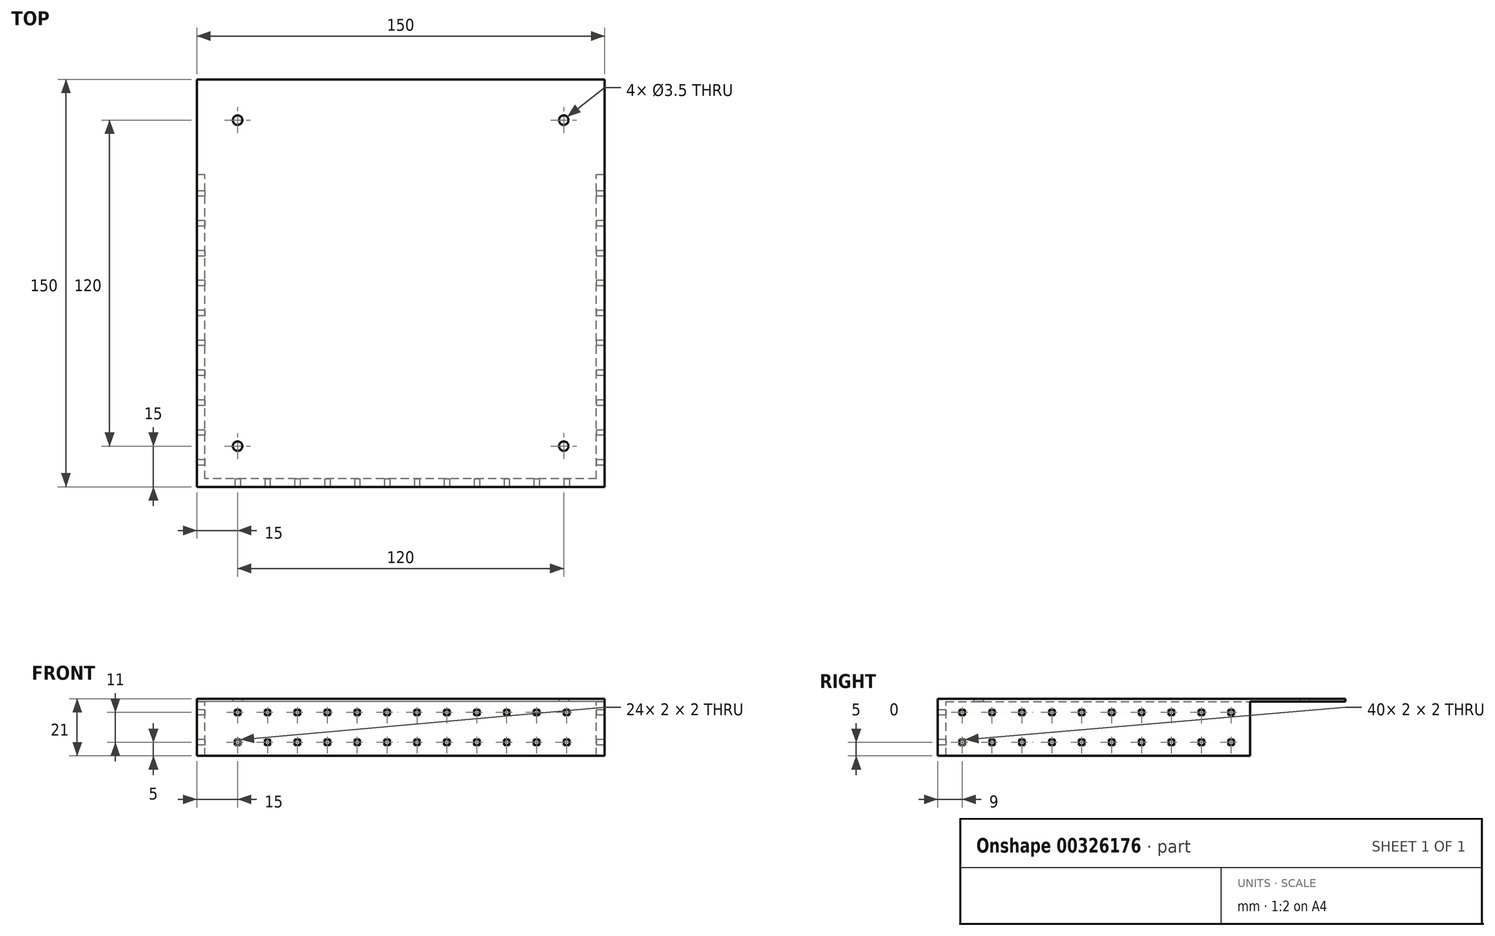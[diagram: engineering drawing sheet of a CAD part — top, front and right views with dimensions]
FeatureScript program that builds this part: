
annotation { "Feature Type Name" : "Feature", "Feature Type Description" : "" }
export const myFeature = defineFeature(function(context is Context, id is Id, definition is map)
    precondition{}
    {
        {
            var Q0;
            Q0=qCreatedBy(makeId("Top.planeOp"),FACE);
            var sketch = newSketch(context, id + "F0", { "sketchPlane" : qUnion([Q0]), "disableImprinting" : false});
            skLineSegment(sketch, "E0.bottom", {"start": v(60, -60) * mm, "end": v(-60, -60) * mm, "construction": true});
            skLineSegment(sketch, "E0.top", {"start": v(60, 60) * mm, "end": v(-60, 60) * mm, "construction": true});
            skLineSegment(sketch, "E0.left", {"start": v(60, -60) * mm, "end": v(60, 60) * mm, "construction": true});
            skLineSegment(sketch, "E0.right", {"start": v(-60, -60) * mm, "end": v(-60, 60) * mm, "construction": true});
            skCircle(sketch, "E1", {"center": v(60, -60) * mm, "radius": 1.75 * mm});
            skCircle(sketch, "E2.1.0", {"center": v(60, 60) * mm, "radius": 1.75 * mm});
            skCircle(sketch, "E2.2.0", {"center": v(-60, 60) * mm, "radius": 1.75 * mm});
            skCircle(sketch, "E2.3.0", {"center": v(-60, -60) * mm, "radius": 1.75 * mm});
            skLineSegment(sketch, "E3.bottom", {"start": v(75, -75) * mm, "end": v(-75, -75) * mm});
            skLineSegment(sketch, "E3.top", {"start": v(75, 75) * mm, "end": v(-75, 75) * mm});
            skLineSegment(sketch, "E3.left", {"start": v(75, -75) * mm, "end": v(75, 75) * mm});
            skLineSegment(sketch, "E3.right", {"start": v(-75, -75) * mm, "end": v(-75, 75) * mm});
            skLineSegment(sketch, "E4.bottom", {"start": v(72, -72) * mm, "end": v(-72, -72) * mm});
            skLineSegment(sketch, "E4.top", {"start": v(72, 72) * mm, "end": v(-72, 72) * mm});
            skLineSegment(sketch, "E4.left", {"start": v(72, -72) * mm, "end": v(72, 72) * mm});
            skLineSegment(sketch, "E4.right", {"start": v(-72, -72) * mm, "end": v(-72, 72) * mm});
            skLineSegment(sketch, "E5", {"start": v(-75, 0) * mm, "end": v(-72, 0) * mm});
            skLineSegment(sketch, "E6", {"start": v(72, 0) * mm, "end": v(75, 0) * mm});
            skLineSegment(sketch, "E7", {"start": v(-75, 40) * mm, "end": v(-72, 40) * mm});
            skLineSegment(sketch, "E8", {"start": v(72, 40) * mm, "end": v(75, 40) * mm});
            skSolve(sketch);
        }
        {
            var Q0;
            Q0=makeQuery(id+"F0.imprint","IMPRINT",FACE,{"disambiguationData":[TD([[makeQuery(id+"F0.imprint","IMPRINT",EDGE,{"derivedFrom":sQuery(id+"F0.wireOp",EDGE,"E1")}),-1.0]])]});
            var Q1;
            {var subQ2=sQuery(id+"F0.wireOp",EDGE,"E3.top");Q1=makeQuery(id+"F0.imprint","IMPRINT",FACE,{"disambiguationData":[TD([[makeQuery(id+"F0.imprint","IMPRINT",EDGE,{"derivedFrom":subQ2}),1.0]])]});}
            var Q2;
            {var subQ2=sQuery(id+"F0.wireOp",EDGE,"E3.bottom");Q2=makeQuery(id+"F0.imprint","IMPRINT",FACE,{"disambiguationData":[TD([[makeQuery(id+"F0.imprint","IMPRINT",EDGE,{"derivedFrom":subQ2}),-1.0]])]});}
            var Q3;
            {var subQ0=sQuery(id+"F0.wireOp",EDGE,"E5");Q3=makeQuery(id+"F0.imprint","IMPRINT",FACE,{"disambiguationData":[TD([[makeQuery(id+"F0.imprint","IMPRINT",EDGE,{"derivedFrom":subQ0}),1.0]])]});}
            var Q4;
            {var subQ0=sQuery(id+"F0.wireOp",EDGE,"E6");Q4=makeQuery(id+"F0.imprint","IMPRINT",FACE,{"disambiguationData":[TD([[makeQuery(id+"F0.imprint","IMPRINT",EDGE,{"derivedFrom":subQ0}),1.0]])]});}
            extrude(context, id + "F1", {"entities" : qUnion([Q0, Q1, Q2, Q3, Q4]), "depth" : 1 * mm});
        }
        {
            var Q0;
            {var subQ2=sQuery(id+"F0.wireOp",EDGE,"E3.bottom");Q0=makeQuery(id+"F0.imprint","IMPRINT",FACE,{"disambiguationData":[TD([[makeQuery(id+"F0.imprint","IMPRINT",EDGE,{"derivedFrom":subQ2}),-1.0]])]});}
            var Q1;
            {var subQ0=sQuery(id+"F0.wireOp",EDGE,"E6");Q1=makeQuery(id+"F0.imprint","IMPRINT",FACE,{"disambiguationData":[TD([[makeQuery(id+"F0.imprint","IMPRINT",EDGE,{"derivedFrom":subQ0}),1.0]])]});}
            var Q2;
            {var subQ0=sQuery(id+"F0.wireOp",EDGE,"E5");Q2=makeQuery(id+"F0.imprint","IMPRINT",FACE,{"disambiguationData":[TD([[makeQuery(id+"F0.imprint","IMPRINT",EDGE,{"derivedFrom":subQ0}),1.0]])]});}
            extrude(context, id + "F2", {"entities" : qUnion([Q0, Q1, Q2]), "operationType" : NewBodyOperationType.ADD, "oppositeDirection" : true, "depth" : 20 * mm});
        }
        {
            var Q0;
            {var subQ0=sQuery(id+"F0.wireOp",EDGE,"E3.right");Q0=makeQuery(id+"F2.boolean.opBoolean","MERGE",FACE,{"derivedFrom":[makeQuery(id+"F1.opExtrude","SWEPT_FACE",FACE,{"disambiguationData":[OSD([subQ0])]}),makeQuery(id+"F2.opExtrude","SWEPT_FACE",FACE,{"disambiguationData":[OSD([subQ0])]})]});}
            var sketch = newSketch(context, id + "F3", { "sketchPlane" : qUnion([Q0])});
            skLineSegment(sketch, "E9.bottom", {"start": v(-32, -5) * mm, "end": v(-34, -5) * mm});
            skLineSegment(sketch, "E9.top", {"start": v(-32, -3) * mm, "end": v(-34, -3) * mm});
            skLineSegment(sketch, "E9.left", {"start": v(-32, -5) * mm, "end": v(-32, -3) * mm});
            skLineSegment(sketch, "E9.right", {"start": v(-34, -5) * mm, "end": v(-34, -3) * mm});
            skPoint(sketch, "E9.middle", {"position": v(-33, -4) * mm});
            skLineSegment(sketch, "E10.0.1.0", {"start": v(-32, -16) * mm, "end": v(-32, -14) * mm});
            skLineSegment(sketch, "E10.0.1.1", {"start": v(-32, -14) * mm, "end": v(-34, -14) * mm});
            skLineSegment(sketch, "E10.0.1.2", {"start": v(-34, -16) * mm, "end": v(-34, -14) * mm});
            skLineSegment(sketch, "E10.0.1.3", {"start": v(-32, -16) * mm, "end": v(-34, -16) * mm});
            skLineSegment(sketch, "E10.1.0.0", {"start": v(-21, -5) * mm, "end": v(-21, -3) * mm});
            skLineSegment(sketch, "E10.1.0.1", {"start": v(-21, -3) * mm, "end": v(-23, -3) * mm});
            skLineSegment(sketch, "E10.1.0.2", {"start": v(-23, -5) * mm, "end": v(-23, -3) * mm});
            skLineSegment(sketch, "E10.1.0.3", {"start": v(-21, -5) * mm, "end": v(-23, -5) * mm});
            skLineSegment(sketch, "E10.1.1.0", {"start": v(-21, -16) * mm, "end": v(-21, -14) * mm});
            skLineSegment(sketch, "E10.1.1.1", {"start": v(-21, -14) * mm, "end": v(-23, -14) * mm});
            skLineSegment(sketch, "E10.1.1.2", {"start": v(-23, -16) * mm, "end": v(-23, -14) * mm});
            skLineSegment(sketch, "E10.1.1.3", {"start": v(-21, -16) * mm, "end": v(-23, -16) * mm});
            skLineSegment(sketch, "E10.2.0.0", {"start": v(-10, -5) * mm, "end": v(-10, -3) * mm});
            skLineSegment(sketch, "E10.2.0.1", {"start": v(-10, -3) * mm, "end": v(-12, -3) * mm});
            skLineSegment(sketch, "E10.2.0.2", {"start": v(-12, -5) * mm, "end": v(-12, -3) * mm});
            skLineSegment(sketch, "E10.2.0.3", {"start": v(-10, -5) * mm, "end": v(-12, -5) * mm});
            skLineSegment(sketch, "E10.2.1.0", {"start": v(-10, -16) * mm, "end": v(-10, -14) * mm});
            skLineSegment(sketch, "E10.2.1.1", {"start": v(-10, -14) * mm, "end": v(-12, -14) * mm});
            skLineSegment(sketch, "E10.2.1.2", {"start": v(-12, -16) * mm, "end": v(-12, -14) * mm});
            skLineSegment(sketch, "E10.2.1.3", {"start": v(-10, -16) * mm, "end": v(-12, -16) * mm});
            skLineSegment(sketch, "E10.3.0.0", {"start": v(1, -5) * mm, "end": v(1, -3) * mm});
            skLineSegment(sketch, "E10.3.0.1", {"start": v(1, -3) * mm, "end": v(-1, -3) * mm});
            skLineSegment(sketch, "E10.3.0.2", {"start": v(-1, -5) * mm, "end": v(-1, -3) * mm});
            skLineSegment(sketch, "E10.3.0.3", {"start": v(1, -5) * mm, "end": v(-1, -5) * mm});
            skLineSegment(sketch, "E10.3.1.0", {"start": v(1, -16) * mm, "end": v(1, -14) * mm});
            skLineSegment(sketch, "E10.3.1.1", {"start": v(1, -14) * mm, "end": v(-1, -14) * mm});
            skLineSegment(sketch, "E10.3.1.2", {"start": v(-1, -16) * mm, "end": v(-1, -14) * mm});
            skLineSegment(sketch, "E10.3.1.3", {"start": v(1, -16) * mm, "end": v(-1, -16) * mm});
            skLineSegment(sketch, "E10.4.0.0", {"start": v(12, -5) * mm, "end": v(12, -3) * mm});
            skLineSegment(sketch, "E10.4.0.1", {"start": v(12, -3) * mm, "end": v(10, -3) * mm});
            skLineSegment(sketch, "E10.4.0.2", {"start": v(10, -5) * mm, "end": v(10, -3) * mm});
            skLineSegment(sketch, "E10.4.0.3", {"start": v(12, -5) * mm, "end": v(10, -5) * mm});
            skLineSegment(sketch, "E10.4.1.0", {"start": v(12, -16) * mm, "end": v(12, -14) * mm});
            skLineSegment(sketch, "E10.4.1.1", {"start": v(12, -14) * mm, "end": v(10, -14) * mm});
            skLineSegment(sketch, "E10.4.1.2", {"start": v(10, -16) * mm, "end": v(10, -14) * mm});
            skLineSegment(sketch, "E10.4.1.3", {"start": v(12, -16) * mm, "end": v(10, -16) * mm});
            skLineSegment(sketch, "E10.5.0.0", {"start": v(23, -5) * mm, "end": v(23, -3) * mm});
            skLineSegment(sketch, "E10.5.0.1", {"start": v(23, -3) * mm, "end": v(21, -3) * mm});
            skLineSegment(sketch, "E10.5.0.2", {"start": v(21, -5) * mm, "end": v(21, -3) * mm});
            skLineSegment(sketch, "E10.5.0.3", {"start": v(23, -5) * mm, "end": v(21, -5) * mm});
            skLineSegment(sketch, "E10.5.1.0", {"start": v(23, -16) * mm, "end": v(23, -14) * mm});
            skLineSegment(sketch, "E10.5.1.1", {"start": v(23, -14) * mm, "end": v(21, -14) * mm});
            skLineSegment(sketch, "E10.5.1.2", {"start": v(21, -16) * mm, "end": v(21, -14) * mm});
            skLineSegment(sketch, "E10.5.1.3", {"start": v(23, -16) * mm, "end": v(21, -16) * mm});
            skLineSegment(sketch, "E10.6.0.0", {"start": v(34, -5) * mm, "end": v(34, -3) * mm});
            skLineSegment(sketch, "E10.6.0.1", {"start": v(34, -3) * mm, "end": v(32, -3) * mm});
            skLineSegment(sketch, "E10.6.0.2", {"start": v(32, -5) * mm, "end": v(32, -3) * mm});
            skLineSegment(sketch, "E10.6.0.3", {"start": v(34, -5) * mm, "end": v(32, -5) * mm});
            skLineSegment(sketch, "E10.6.1.0", {"start": v(34, -16) * mm, "end": v(34, -14) * mm});
            skLineSegment(sketch, "E10.6.1.1", {"start": v(34, -14) * mm, "end": v(32, -14) * mm});
            skLineSegment(sketch, "E10.6.1.2", {"start": v(32, -16) * mm, "end": v(32, -14) * mm});
            skLineSegment(sketch, "E10.6.1.3", {"start": v(34, -16) * mm, "end": v(32, -16) * mm});
            skLineSegment(sketch, "E10.7.0.0", {"start": v(45, -5) * mm, "end": v(45, -3) * mm});
            skLineSegment(sketch, "E10.7.0.1", {"start": v(45, -3) * mm, "end": v(43, -3) * mm});
            skLineSegment(sketch, "E10.7.0.2", {"start": v(43, -5) * mm, "end": v(43, -3) * mm});
            skLineSegment(sketch, "E10.7.0.3", {"start": v(45, -5) * mm, "end": v(43, -5) * mm});
            skLineSegment(sketch, "E10.7.1.0", {"start": v(45, -16) * mm, "end": v(45, -14) * mm});
            skLineSegment(sketch, "E10.7.1.1", {"start": v(45, -14) * mm, "end": v(43, -14) * mm});
            skLineSegment(sketch, "E10.7.1.2", {"start": v(43, -16) * mm, "end": v(43, -14) * mm});
            skLineSegment(sketch, "E10.7.1.3", {"start": v(45, -16) * mm, "end": v(43, -16) * mm});
            skLineSegment(sketch, "E10.8.0.0", {"start": v(56, -5) * mm, "end": v(56, -3) * mm});
            skLineSegment(sketch, "E10.8.0.1", {"start": v(56, -3) * mm, "end": v(54, -3) * mm});
            skLineSegment(sketch, "E10.8.0.2", {"start": v(54, -5) * mm, "end": v(54, -3) * mm});
            skLineSegment(sketch, "E10.8.0.3", {"start": v(56, -5) * mm, "end": v(54, -5) * mm});
            skLineSegment(sketch, "E10.8.1.0", {"start": v(56, -16) * mm, "end": v(56, -14) * mm});
            skLineSegment(sketch, "E10.8.1.1", {"start": v(56, -14) * mm, "end": v(54, -14) * mm});
            skLineSegment(sketch, "E10.8.1.2", {"start": v(54, -16) * mm, "end": v(54, -14) * mm});
            skLineSegment(sketch, "E10.8.1.3", {"start": v(56, -16) * mm, "end": v(54, -16) * mm});
            skLineSegment(sketch, "E10.9.0.0", {"start": v(67, -5) * mm, "end": v(67, -3) * mm});
            skLineSegment(sketch, "E10.9.0.1", {"start": v(67, -3) * mm, "end": v(65, -3) * mm});
            skLineSegment(sketch, "E10.9.0.2", {"start": v(65, -5) * mm, "end": v(65, -3) * mm});
            skLineSegment(sketch, "E10.9.0.3", {"start": v(67, -5) * mm, "end": v(65, -5) * mm});
            skLineSegment(sketch, "E10.9.1.0", {"start": v(67, -16) * mm, "end": v(67, -14) * mm});
            skLineSegment(sketch, "E10.9.1.1", {"start": v(67, -14) * mm, "end": v(65, -14) * mm});
            skLineSegment(sketch, "E10.9.1.2", {"start": v(65, -16) * mm, "end": v(65, -14) * mm});
            skLineSegment(sketch, "E10.9.1.3", {"start": v(67, -16) * mm, "end": v(65, -16) * mm});
            skLineSegment(sketch, "E10.direction1", {"start": v(-32, -5) * mm, "end": v(-21, -5) * mm, "construction": true});
            skLineSegment(sketch, "E10.direction2", {"start": v(-32, -5) * mm, "end": v(-32, -16) * mm, "construction": true});
            skSolve(sketch);
        }
        {
            var Q0;
            Q0=makeQuery(id+"F3.imprint","IMPRINT",FACE,{"disambiguationData":[TD([[makeQuery(id+"F3.imprint","IMPRINT",EDGE,{"derivedFrom":sQuery(id+"F3.wireOp",EDGE,"E9.bottom")}),-1.0]])]});
            var Q1;
            Q1=makeQuery(id+"F3.imprint","IMPRINT",FACE,{"disambiguationData":[TD([[makeQuery(id+"F3.imprint","IMPRINT",EDGE,{"derivedFrom":sQuery(id+"F3.wireOp",EDGE,"E10.0.1.0")}),1.0]])]});
            var Q2;
            Q2=makeQuery(id+"F3.imprint","IMPRINT",FACE,{"disambiguationData":[TD([[makeQuery(id+"F3.imprint","IMPRINT",EDGE,{"derivedFrom":sQuery(id+"F3.wireOp",EDGE,"E10.1.0.0")}),1.0]])]});
            var Q3;
            Q3=makeQuery(id+"F3.imprint","IMPRINT",FACE,{"disambiguationData":[TD([[makeQuery(id+"F3.imprint","IMPRINT",EDGE,{"derivedFrom":sQuery(id+"F3.wireOp",EDGE,"E10.2.0.0")}),1.0]])]});
            var Q4;
            Q4=makeQuery(id+"F3.imprint","IMPRINT",FACE,{"disambiguationData":[TD([[makeQuery(id+"F3.imprint","IMPRINT",EDGE,{"derivedFrom":sQuery(id+"F3.wireOp",EDGE,"E10.2.1.0")}),1.0]])]});
            var Q5;
            Q5=makeQuery(id+"F3.imprint","IMPRINT",FACE,{"disambiguationData":[TD([[makeQuery(id+"F3.imprint","IMPRINT",EDGE,{"derivedFrom":sQuery(id+"F3.wireOp",EDGE,"E10.1.1.0")}),1.0]])]});
            var Q6;
            Q6=makeQuery(id+"F3.imprint","IMPRINT",FACE,{"disambiguationData":[TD([[makeQuery(id+"F3.imprint","IMPRINT",EDGE,{"derivedFrom":sQuery(id+"F3.wireOp",EDGE,"E10.3.1.0")}),1.0]])]});
            var Q7;
            Q7=makeQuery(id+"F3.imprint","IMPRINT",FACE,{"disambiguationData":[TD([[makeQuery(id+"F3.imprint","IMPRINT",EDGE,{"derivedFrom":sQuery(id+"F3.wireOp",EDGE,"E10.4.1.0")}),1.0]])]});
            var Q8;
            Q8=makeQuery(id+"F3.imprint","IMPRINT",FACE,{"disambiguationData":[TD([[makeQuery(id+"F3.imprint","IMPRINT",EDGE,{"derivedFrom":sQuery(id+"F3.wireOp",EDGE,"E10.5.1.0")}),1.0]])]});
            var Q9;
            Q9=makeQuery(id+"F3.imprint","IMPRINT",FACE,{"disambiguationData":[TD([[makeQuery(id+"F3.imprint","IMPRINT",EDGE,{"derivedFrom":sQuery(id+"F3.wireOp",EDGE,"E10.6.1.0")}),1.0]])]});
            var Q10;
            Q10=makeQuery(id+"F3.imprint","IMPRINT",FACE,{"disambiguationData":[TD([[makeQuery(id+"F3.imprint","IMPRINT",EDGE,{"derivedFrom":sQuery(id+"F3.wireOp",EDGE,"E10.7.1.0")}),1.0]])]});
            var Q11;
            Q11=makeQuery(id+"F3.imprint","IMPRINT",FACE,{"disambiguationData":[TD([[makeQuery(id+"F3.imprint","IMPRINT",EDGE,{"derivedFrom":sQuery(id+"F3.wireOp",EDGE,"E10.8.1.0")}),1.0]])]});
            var Q12;
            Q12=makeQuery(id+"F3.imprint","IMPRINT",FACE,{"disambiguationData":[TD([[makeQuery(id+"F3.imprint","IMPRINT",EDGE,{"derivedFrom":sQuery(id+"F3.wireOp",EDGE,"E10.9.1.0")}),1.0]])]});
            var Q13;
            Q13=makeQuery(id+"F3.imprint","IMPRINT",FACE,{"disambiguationData":[TD([[makeQuery(id+"F3.imprint","IMPRINT",EDGE,{"derivedFrom":sQuery(id+"F3.wireOp",EDGE,"E10.9.0.0")}),1.0]])]});
            var Q14;
            Q14=makeQuery(id+"F3.imprint","IMPRINT",FACE,{"disambiguationData":[TD([[makeQuery(id+"F3.imprint","IMPRINT",EDGE,{"derivedFrom":sQuery(id+"F3.wireOp",EDGE,"E10.8.0.0")}),1.0]])]});
            var Q15;
            Q15=makeQuery(id+"F3.imprint","IMPRINT",FACE,{"disambiguationData":[TD([[makeQuery(id+"F3.imprint","IMPRINT",EDGE,{"derivedFrom":sQuery(id+"F3.wireOp",EDGE,"E10.7.0.0")}),1.0]])]});
            var Q16;
            Q16=makeQuery(id+"F3.imprint","IMPRINT",FACE,{"disambiguationData":[TD([[makeQuery(id+"F3.imprint","IMPRINT",EDGE,{"derivedFrom":sQuery(id+"F3.wireOp",EDGE,"E10.6.0.0")}),1.0]])]});
            var Q17;
            Q17=makeQuery(id+"F3.imprint","IMPRINT",FACE,{"disambiguationData":[TD([[makeQuery(id+"F3.imprint","IMPRINT",EDGE,{"derivedFrom":sQuery(id+"F3.wireOp",EDGE,"E10.5.0.0")}),1.0]])]});
            var Q18;
            Q18=makeQuery(id+"F3.imprint","IMPRINT",FACE,{"disambiguationData":[TD([[makeQuery(id+"F3.imprint","IMPRINT",EDGE,{"derivedFrom":sQuery(id+"F3.wireOp",EDGE,"E10.4.0.0")}),1.0]])]});
            var Q19;
            Q19=makeQuery(id+"F3.imprint","IMPRINT",FACE,{"disambiguationData":[TD([[makeQuery(id+"F3.imprint","IMPRINT",EDGE,{"derivedFrom":sQuery(id+"F3.wireOp",EDGE,"E10.3.0.0")}),1.0]])]});
            extrude(context, id + "F4", {"entities" : qUnion([Q0, Q1, Q2, Q3, Q4, Q5, Q6, Q7, Q8, Q9, Q10, Q11, Q12, Q13, Q14, Q15, Q16, Q17, Q18, Q19]), "operationType" : NewBodyOperationType.REMOVE, "oppositeDirection" : true, "depth" : 200 * mm});
        }
        {
            var Q0;
            {var subQ0=sQuery(id+"F0.wireOp",EDGE,"E3.bottom");Q0=makeQuery(id+"F2.boolean.opBoolean","MERGE",FACE,{"derivedFrom":[makeQuery(id+"F1.opExtrude","SWEPT_FACE",FACE,{"disambiguationData":[OSD([subQ0])]}),makeQuery(id+"F2.opExtrude","SWEPT_FACE",FACE,{"disambiguationData":[OSD([subQ0])]})]});}
            var sketch = newSketch(context, id + "F5", { "sketchPlane" : qUnion([Q0])});
            skLineSegment(sketch, "E11.bottom", {"start": v(-59, -5) * mm, "end": v(-61, -5) * mm});
            skLineSegment(sketch, "E11.top", {"start": v(-59, -3) * mm, "end": v(-61, -3) * mm});
            skLineSegment(sketch, "E11.left", {"start": v(-59, -5) * mm, "end": v(-59, -3) * mm});
            skLineSegment(sketch, "E11.right", {"start": v(-61, -5) * mm, "end": v(-61, -3) * mm});
            skPoint(sketch, "E11.middle", {"position": v(-60, -4) * mm});
            skLineSegment(sketch, "E12.0.1.0", {"start": v(-59, -16) * mm, "end": v(-59, -14) * mm});
            skLineSegment(sketch, "E12.0.1.1", {"start": v(-59, -14) * mm, "end": v(-61, -14) * mm});
            skLineSegment(sketch, "E12.0.1.2", {"start": v(-61, -16) * mm, "end": v(-61, -14) * mm});
            skLineSegment(sketch, "E12.0.1.3", {"start": v(-59, -16) * mm, "end": v(-61, -16) * mm});
            skLineSegment(sketch, "E12.1.0.0", {"start": v(-48, -5) * mm, "end": v(-48, -3) * mm});
            skLineSegment(sketch, "E12.1.0.1", {"start": v(-48, -3) * mm, "end": v(-50, -3) * mm});
            skLineSegment(sketch, "E12.1.0.2", {"start": v(-50, -5) * mm, "end": v(-50, -3) * mm});
            skLineSegment(sketch, "E12.1.0.3", {"start": v(-48, -5) * mm, "end": v(-50, -5) * mm});
            skLineSegment(sketch, "E12.1.1.0", {"start": v(-48, -16) * mm, "end": v(-48, -14) * mm});
            skLineSegment(sketch, "E12.1.1.1", {"start": v(-48, -14) * mm, "end": v(-50, -14) * mm});
            skLineSegment(sketch, "E12.1.1.2", {"start": v(-50, -16) * mm, "end": v(-50, -14) * mm});
            skLineSegment(sketch, "E12.1.1.3", {"start": v(-48, -16) * mm, "end": v(-50, -16) * mm});
            skLineSegment(sketch, "E12.2.0.0", {"start": v(-37, -5) * mm, "end": v(-37, -3) * mm});
            skLineSegment(sketch, "E12.2.0.1", {"start": v(-37, -3) * mm, "end": v(-39, -3) * mm});
            skLineSegment(sketch, "E12.2.0.2", {"start": v(-39, -5) * mm, "end": v(-39, -3) * mm});
            skLineSegment(sketch, "E12.2.0.3", {"start": v(-37, -5) * mm, "end": v(-39, -5) * mm});
            skLineSegment(sketch, "E12.2.1.0", {"start": v(-37, -16) * mm, "end": v(-37, -14) * mm});
            skLineSegment(sketch, "E12.2.1.1", {"start": v(-37, -14) * mm, "end": v(-39, -14) * mm});
            skLineSegment(sketch, "E12.2.1.2", {"start": v(-39, -16) * mm, "end": v(-39, -14) * mm});
            skLineSegment(sketch, "E12.2.1.3", {"start": v(-37, -16) * mm, "end": v(-39, -16) * mm});
            skLineSegment(sketch, "E12.3.0.0", {"start": v(-26, -5) * mm, "end": v(-26, -3) * mm});
            skLineSegment(sketch, "E12.3.0.1", {"start": v(-26, -3) * mm, "end": v(-28, -3) * mm});
            skLineSegment(sketch, "E12.3.0.2", {"start": v(-28, -5) * mm, "end": v(-28, -3) * mm});
            skLineSegment(sketch, "E12.3.0.3", {"start": v(-26, -5) * mm, "end": v(-28, -5) * mm});
            skLineSegment(sketch, "E12.3.1.0", {"start": v(-26, -16) * mm, "end": v(-26, -14) * mm});
            skLineSegment(sketch, "E12.3.1.1", {"start": v(-26, -14) * mm, "end": v(-28, -14) * mm});
            skLineSegment(sketch, "E12.3.1.2", {"start": v(-28, -16) * mm, "end": v(-28, -14) * mm});
            skLineSegment(sketch, "E12.3.1.3", {"start": v(-26, -16) * mm, "end": v(-28, -16) * mm});
            skLineSegment(sketch, "E12.4.0.0", {"start": v(-15, -5) * mm, "end": v(-15, -3) * mm});
            skLineSegment(sketch, "E12.4.0.1", {"start": v(-15, -3) * mm, "end": v(-17, -3) * mm});
            skLineSegment(sketch, "E12.4.0.2", {"start": v(-17, -5) * mm, "end": v(-17, -3) * mm});
            skLineSegment(sketch, "E12.4.0.3", {"start": v(-15, -5) * mm, "end": v(-17, -5) * mm});
            skLineSegment(sketch, "E12.4.1.0", {"start": v(-15, -16) * mm, "end": v(-15, -14) * mm});
            skLineSegment(sketch, "E12.4.1.1", {"start": v(-15, -14) * mm, "end": v(-17, -14) * mm});
            skLineSegment(sketch, "E12.4.1.2", {"start": v(-17, -16) * mm, "end": v(-17, -14) * mm});
            skLineSegment(sketch, "E12.4.1.3", {"start": v(-15, -16) * mm, "end": v(-17, -16) * mm});
            skLineSegment(sketch, "E12.5.0.0", {"start": v(-4, -5) * mm, "end": v(-4, -3) * mm});
            skLineSegment(sketch, "E12.5.0.1", {"start": v(-4, -3) * mm, "end": v(-6, -3) * mm});
            skLineSegment(sketch, "E12.5.0.2", {"start": v(-6, -5) * mm, "end": v(-6, -3) * mm});
            skLineSegment(sketch, "E12.5.0.3", {"start": v(-4, -5) * mm, "end": v(-6, -5) * mm});
            skLineSegment(sketch, "E12.5.1.0", {"start": v(-4, -16) * mm, "end": v(-4, -14) * mm});
            skLineSegment(sketch, "E12.5.1.1", {"start": v(-4, -14) * mm, "end": v(-6, -14) * mm});
            skLineSegment(sketch, "E12.5.1.2", {"start": v(-6, -16) * mm, "end": v(-6, -14) * mm});
            skLineSegment(sketch, "E12.5.1.3", {"start": v(-4, -16) * mm, "end": v(-6, -16) * mm});
            skLineSegment(sketch, "E12.6.0.0", {"start": v(7, -5) * mm, "end": v(7, -3) * mm});
            skLineSegment(sketch, "E12.6.0.1", {"start": v(7, -3) * mm, "end": v(5, -3) * mm});
            skLineSegment(sketch, "E12.6.0.2", {"start": v(5, -5) * mm, "end": v(5, -3) * mm});
            skLineSegment(sketch, "E12.6.0.3", {"start": v(7, -5) * mm, "end": v(5, -5) * mm});
            skLineSegment(sketch, "E12.6.1.0", {"start": v(7, -16) * mm, "end": v(7, -14) * mm});
            skLineSegment(sketch, "E12.6.1.1", {"start": v(7, -14) * mm, "end": v(5, -14) * mm});
            skLineSegment(sketch, "E12.6.1.2", {"start": v(5, -16) * mm, "end": v(5, -14) * mm});
            skLineSegment(sketch, "E12.6.1.3", {"start": v(7, -16) * mm, "end": v(5, -16) * mm});
            skLineSegment(sketch, "E12.7.0.0", {"start": v(18, -5) * mm, "end": v(18, -3) * mm});
            skLineSegment(sketch, "E12.7.0.1", {"start": v(18, -3) * mm, "end": v(16, -3) * mm});
            skLineSegment(sketch, "E12.7.0.2", {"start": v(16, -5) * mm, "end": v(16, -3) * mm});
            skLineSegment(sketch, "E12.7.0.3", {"start": v(18, -5) * mm, "end": v(16, -5) * mm});
            skLineSegment(sketch, "E12.7.1.0", {"start": v(18, -16) * mm, "end": v(18, -14) * mm});
            skLineSegment(sketch, "E12.7.1.1", {"start": v(18, -14) * mm, "end": v(16, -14) * mm});
            skLineSegment(sketch, "E12.7.1.2", {"start": v(16, -16) * mm, "end": v(16, -14) * mm});
            skLineSegment(sketch, "E12.7.1.3", {"start": v(18, -16) * mm, "end": v(16, -16) * mm});
            skLineSegment(sketch, "E12.8.0.0", {"start": v(29, -5) * mm, "end": v(29, -3) * mm});
            skLineSegment(sketch, "E12.8.0.1", {"start": v(29, -3) * mm, "end": v(27, -3) * mm});
            skLineSegment(sketch, "E12.8.0.2", {"start": v(27, -5) * mm, "end": v(27, -3) * mm});
            skLineSegment(sketch, "E12.8.0.3", {"start": v(29, -5) * mm, "end": v(27, -5) * mm});
            skLineSegment(sketch, "E12.8.1.0", {"start": v(29, -16) * mm, "end": v(29, -14) * mm});
            skLineSegment(sketch, "E12.8.1.1", {"start": v(29, -14) * mm, "end": v(27, -14) * mm});
            skLineSegment(sketch, "E12.8.1.2", {"start": v(27, -16) * mm, "end": v(27, -14) * mm});
            skLineSegment(sketch, "E12.8.1.3", {"start": v(29, -16) * mm, "end": v(27, -16) * mm});
            skLineSegment(sketch, "E12.9.0.0", {"start": v(40, -5) * mm, "end": v(40, -3) * mm});
            skLineSegment(sketch, "E12.9.0.1", {"start": v(40, -3) * mm, "end": v(38, -3) * mm});
            skLineSegment(sketch, "E12.9.0.2", {"start": v(38, -5) * mm, "end": v(38, -3) * mm});
            skLineSegment(sketch, "E12.9.0.3", {"start": v(40, -5) * mm, "end": v(38, -5) * mm});
            skLineSegment(sketch, "E12.9.1.0", {"start": v(40, -16) * mm, "end": v(40, -14) * mm});
            skLineSegment(sketch, "E12.9.1.1", {"start": v(40, -14) * mm, "end": v(38, -14) * mm});
            skLineSegment(sketch, "E12.9.1.2", {"start": v(38, -16) * mm, "end": v(38, -14) * mm});
            skLineSegment(sketch, "E12.9.1.3", {"start": v(40, -16) * mm, "end": v(38, -16) * mm});
            skLineSegment(sketch, "E12.direction1", {"start": v(-59, -5) * mm, "end": v(-48, -5) * mm, "construction": true});
            skLineSegment(sketch, "E12.direction2", {"start": v(-59, -5) * mm, "end": v(-59, -16) * mm, "construction": true});
            skLineSegment(sketch, "E13.0.10.0", {"start": v(51, -5) * mm, "end": v(51, -3) * mm});
            skLineSegment(sketch, "E13.3.10.0", {"start": v(51, -3) * mm, "end": v(49, -3) * mm});
            skLineSegment(sketch, "E13.6.10.0", {"start": v(49, -5) * mm, "end": v(49, -3) * mm});
            skLineSegment(sketch, "E13.9.10.0", {"start": v(51, -5) * mm, "end": v(49, -5) * mm});
            skLineSegment(sketch, "E13.0.10.1", {"start": v(51, -16) * mm, "end": v(51, -14) * mm});
            skLineSegment(sketch, "E13.3.10.1", {"start": v(51, -14) * mm, "end": v(49, -14) * mm});
            skLineSegment(sketch, "E13.6.10.1", {"start": v(49, -16) * mm, "end": v(49, -14) * mm});
            skLineSegment(sketch, "E13.9.10.1", {"start": v(51, -16) * mm, "end": v(49, -16) * mm});
            skLineSegment(sketch, "E14.0.11.0", {"start": v(62, -5) * mm, "end": v(62, -3) * mm});
            skLineSegment(sketch, "E14.3.11.0", {"start": v(62, -3) * mm, "end": v(60, -3) * mm});
            skLineSegment(sketch, "E14.6.11.0", {"start": v(60, -5) * mm, "end": v(60, -3) * mm});
            skLineSegment(sketch, "E14.9.11.0", {"start": v(62, -5) * mm, "end": v(60, -5) * mm});
            skLineSegment(sketch, "E14.0.11.1", {"start": v(62, -16) * mm, "end": v(62, -14) * mm});
            skLineSegment(sketch, "E14.3.11.1", {"start": v(62, -14) * mm, "end": v(60, -14) * mm});
            skLineSegment(sketch, "E14.6.11.1", {"start": v(60, -16) * mm, "end": v(60, -14) * mm});
            skLineSegment(sketch, "E14.9.11.1", {"start": v(62, -16) * mm, "end": v(60, -16) * mm});
            skSolve(sketch);
        }
        {
            var Q0;
            Q0=makeQuery(id+"F5.imprint","IMPRINT",FACE,{"disambiguationData":[TD([[makeQuery(id+"F5.imprint","IMPRINT",EDGE,{"derivedFrom":sQuery(id+"F5.wireOp",EDGE,"E11.bottom")}),-1.0]])]});
            var Q1;
            Q1=makeQuery(id+"F5.imprint","IMPRINT",FACE,{"disambiguationData":[TD([[makeQuery(id+"F5.imprint","IMPRINT",EDGE,{"derivedFrom":sQuery(id+"F5.wireOp",EDGE,"E12.0.1.0")}),1.0]])]});
            var Q2;
            Q2=makeQuery(id+"F5.imprint","IMPRINT",FACE,{"disambiguationData":[TD([[makeQuery(id+"F5.imprint","IMPRINT",EDGE,{"derivedFrom":sQuery(id+"F5.wireOp",EDGE,"E12.1.0.0")}),1.0]])]});
            var Q3;
            Q3=makeQuery(id+"F5.imprint","IMPRINT",FACE,{"disambiguationData":[TD([[makeQuery(id+"F5.imprint","IMPRINT",EDGE,{"derivedFrom":sQuery(id+"F5.wireOp",EDGE,"E12.1.1.0")}),1.0]])]});
            var Q4;
            Q4=makeQuery(id+"F5.imprint","IMPRINT",FACE,{"disambiguationData":[TD([[makeQuery(id+"F5.imprint","IMPRINT",EDGE,{"derivedFrom":sQuery(id+"F5.wireOp",EDGE,"E12.2.0.0")}),1.0]])]});
            var Q5;
            Q5=makeQuery(id+"F5.imprint","IMPRINT",FACE,{"disambiguationData":[TD([[makeQuery(id+"F5.imprint","IMPRINT",EDGE,{"derivedFrom":sQuery(id+"F5.wireOp",EDGE,"E12.2.1.0")}),1.0]])]});
            var Q6;
            Q6=makeQuery(id+"F5.imprint","IMPRINT",FACE,{"disambiguationData":[TD([[makeQuery(id+"F5.imprint","IMPRINT",EDGE,{"derivedFrom":sQuery(id+"F5.wireOp",EDGE,"E12.3.0.0")}),1.0]])]});
            var Q7;
            Q7=makeQuery(id+"F5.imprint","IMPRINT",FACE,{"disambiguationData":[TD([[makeQuery(id+"F5.imprint","IMPRINT",EDGE,{"derivedFrom":sQuery(id+"F5.wireOp",EDGE,"E12.4.0.0")}),1.0]])]});
            var Q8;
            Q8=makeQuery(id+"F5.imprint","IMPRINT",FACE,{"disambiguationData":[TD([[makeQuery(id+"F5.imprint","IMPRINT",EDGE,{"derivedFrom":sQuery(id+"F5.wireOp",EDGE,"E12.5.0.0")}),1.0]])]});
            var Q9;
            Q9=makeQuery(id+"F5.imprint","IMPRINT",FACE,{"disambiguationData":[TD([[makeQuery(id+"F5.imprint","IMPRINT",EDGE,{"derivedFrom":sQuery(id+"F5.wireOp",EDGE,"E12.6.0.0")}),1.0]])]});
            var Q10;
            Q10=makeQuery(id+"F5.imprint","IMPRINT",FACE,{"disambiguationData":[TD([[makeQuery(id+"F5.imprint","IMPRINT",EDGE,{"derivedFrom":sQuery(id+"F5.wireOp",EDGE,"E12.7.0.0")}),1.0]])]});
            var Q11;
            Q11=makeQuery(id+"F5.imprint","IMPRINT",FACE,{"disambiguationData":[TD([[makeQuery(id+"F5.imprint","IMPRINT",EDGE,{"derivedFrom":sQuery(id+"F5.wireOp",EDGE,"E12.8.0.0")}),1.0]])]});
            var Q12;
            Q12=makeQuery(id+"F5.imprint","IMPRINT",FACE,{"disambiguationData":[TD([[makeQuery(id+"F5.imprint","IMPRINT",EDGE,{"derivedFrom":sQuery(id+"F5.wireOp",EDGE,"E12.9.0.0")}),1.0]])]});
            var Q13;
            Q13=makeQuery(id+"F5.imprint","IMPRINT",FACE,{"disambiguationData":[TD([[makeQuery(id+"F5.imprint","IMPRINT",EDGE,{"derivedFrom":sQuery(id+"F5.wireOp",EDGE,"E13.0.10.0")}),1.0]])]});
            var Q14;
            Q14=makeQuery(id+"F5.imprint","IMPRINT",FACE,{"disambiguationData":[TD([[makeQuery(id+"F5.imprint","IMPRINT",EDGE,{"derivedFrom":sQuery(id+"F5.wireOp",EDGE,"E14.0.11.0")}),1.0]])]});
            var Q15;
            Q15=makeQuery(id+"F5.imprint","IMPRINT",FACE,{"disambiguationData":[TD([[makeQuery(id+"F5.imprint","IMPRINT",EDGE,{"derivedFrom":sQuery(id+"F5.wireOp",EDGE,"E14.0.11.1")}),1.0]])]});
            var Q16;
            Q16=makeQuery(id+"F5.imprint","IMPRINT",FACE,{"disambiguationData":[TD([[makeQuery(id+"F5.imprint","IMPRINT",EDGE,{"derivedFrom":sQuery(id+"F5.wireOp",EDGE,"E13.0.10.1")}),1.0]])]});
            var Q17;
            Q17=makeQuery(id+"F5.imprint","IMPRINT",FACE,{"disambiguationData":[TD([[makeQuery(id+"F5.imprint","IMPRINT",EDGE,{"derivedFrom":sQuery(id+"F5.wireOp",EDGE,"E12.9.1.0")}),1.0]])]});
            var Q18;
            Q18=makeQuery(id+"F5.imprint","IMPRINT",FACE,{"disambiguationData":[TD([[makeQuery(id+"F5.imprint","IMPRINT",EDGE,{"derivedFrom":sQuery(id+"F5.wireOp",EDGE,"E12.8.1.0")}),1.0]])]});
            var Q19;
            Q19=makeQuery(id+"F5.imprint","IMPRINT",FACE,{"disambiguationData":[TD([[makeQuery(id+"F5.imprint","IMPRINT",EDGE,{"derivedFrom":sQuery(id+"F5.wireOp",EDGE,"E12.7.1.0")}),1.0]])]});
            var Q20;
            Q20=makeQuery(id+"F5.imprint","IMPRINT",FACE,{"disambiguationData":[TD([[makeQuery(id+"F5.imprint","IMPRINT",EDGE,{"derivedFrom":sQuery(id+"F5.wireOp",EDGE,"E12.6.1.0")}),1.0]])]});
            var Q21;
            Q21=makeQuery(id+"F5.imprint","IMPRINT",FACE,{"disambiguationData":[TD([[makeQuery(id+"F5.imprint","IMPRINT",EDGE,{"derivedFrom":sQuery(id+"F5.wireOp",EDGE,"E12.5.1.0")}),1.0]])]});
            var Q22;
            Q22=makeQuery(id+"F5.imprint","IMPRINT",FACE,{"disambiguationData":[TD([[makeQuery(id+"F5.imprint","IMPRINT",EDGE,{"derivedFrom":sQuery(id+"F5.wireOp",EDGE,"E12.4.1.0")}),1.0]])]});
            var Q23;
            Q23=makeQuery(id+"F5.imprint","IMPRINT",FACE,{"disambiguationData":[TD([[makeQuery(id+"F5.imprint","IMPRINT",EDGE,{"derivedFrom":sQuery(id+"F5.wireOp",EDGE,"E12.3.1.0")}),1.0]])]});
            extrude(context, id + "F6", {"entities" : qUnion([Q0, Q1, Q2, Q3, Q4, Q5, Q6, Q7, Q8, Q9, Q10, Q11, Q12, Q13, Q14, Q15, Q16, Q17, Q18, Q19, Q20, Q21, Q22, Q23]), "operationType" : NewBodyOperationType.REMOVE, "oppositeDirection" : true, "depth" : 25 * mm});
        }
    });
